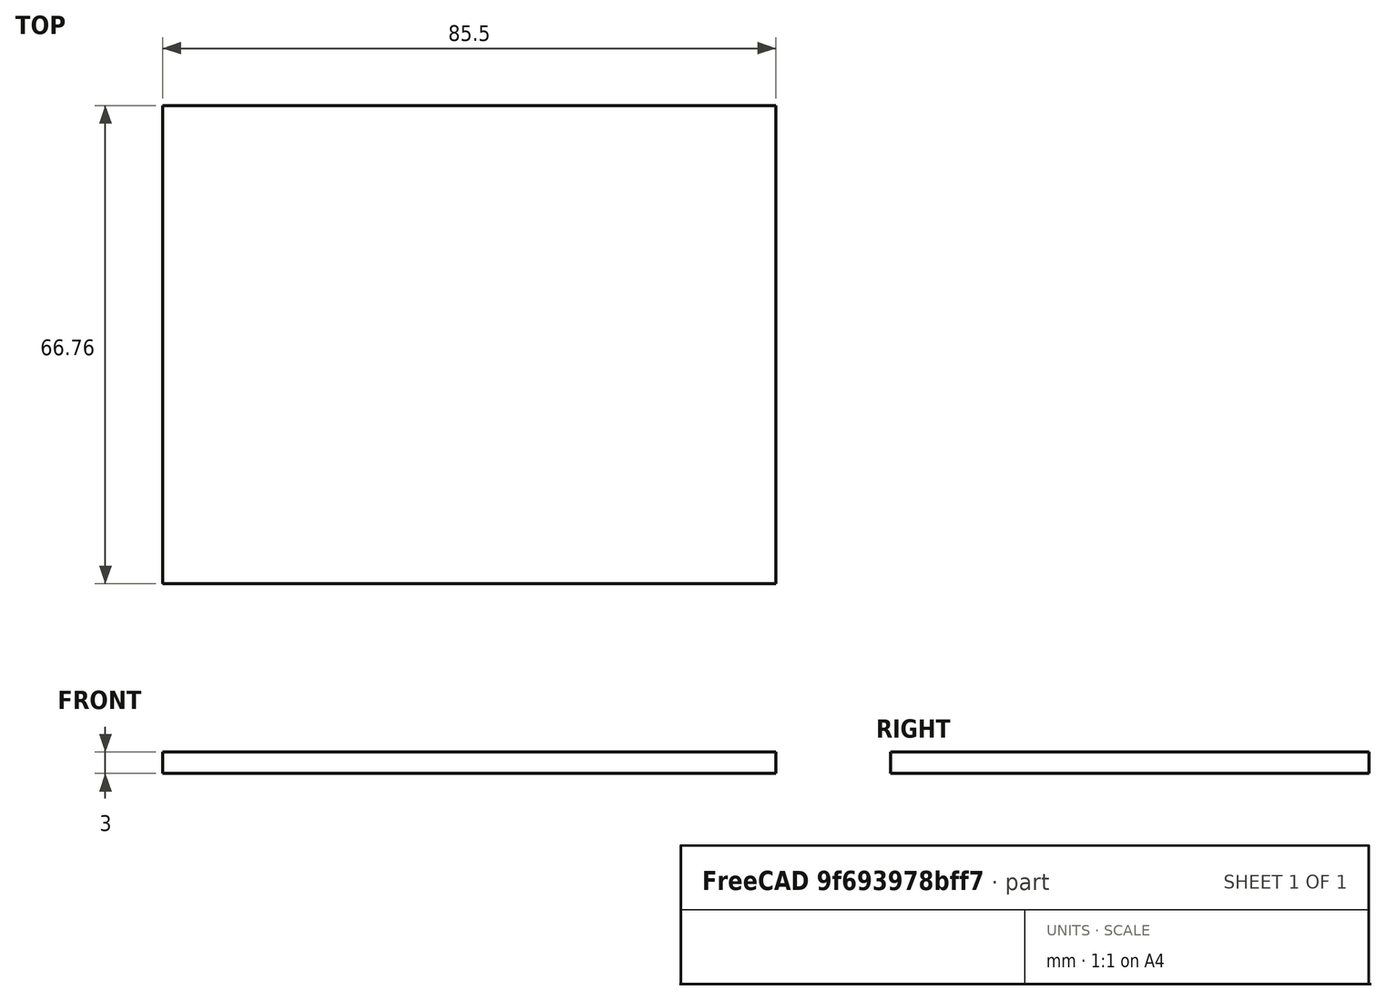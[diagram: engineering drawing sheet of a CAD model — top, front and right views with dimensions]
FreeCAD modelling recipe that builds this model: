
FCSTD DOCUMENT  (FreeCAD 1.0R39109 (Git))
Label: pcb
License: All rights reserved
LicenseURL: http://en.wikipedia.org/wiki/All_rights_reserved
objects: Sketcher::SketchObject×2, PartDesign::Pad×1, PartDesign::Body×1, App::VarSet×1
note: 8 computed .brp shape members not serialized (recipe doc carries the construction recipe); baked Part::Feature solids carry a one-line shape summary decoded from their .brp

FEATURE [Sketcher::SketchObject] Sketch
  ArcFitTolerance = 0
  AttachmentSupport = -> [XY_Plane]
  FullyConstrained = true
  MakeInternals = false
  MapMode = 5
  expr: Constraints[10] = VarSet.PCB_Width
  expr: Constraints[9] = VarSet.Ppt_PCB_Len
  sketch-geometry (4):
    g0: LineSegment StartX=-42.75 StartY=33.375 StartZ=0 EndX=42.75 EndY=33.375 EndZ=0
    g1: LineSegment StartX=42.75 StartY=33.375 StartZ=0 EndX=42.75 EndY=-33.375 EndZ=0
    g2: LineSegment StartX=42.75 StartY=-33.375 StartZ=0 EndX=-42.75 EndY=-33.375 EndZ=0
    g3: LineSegment StartX=-42.75 StartY=-33.375 StartZ=0 EndX=-42.75 EndY=33.375 EndZ=0
  constraints (11):
    c: Coincident(g0,g1)
    c: Coincident(g1,g2)
    c: Coincident(g2,g3)
    c: Coincident(g3,g0)
    c: Horizontal(g0)
    c: Horizontal(g2)
    c: Vertical(g1)
    c: Vertical(g3)
    c: Symmetric(g0,g1,g-1)
    c: DistanceX(g0,g0) = 85.5
    c: DistanceY(g1,g1) = 66.75
FEATURE [PartDesign::Pad] Pad
  Direction = (0,0,1)
  Length = 3
  Length2 = 10
  Profile = -> Sketch
  ReferenceAxis = -> Sketch [N_Axis]
  Suppressed = false
  Type = 0
FEATURE [Sketcher::SketchObject] Sketch001
  ArcFitTolerance = 0
  AttachmentSupport = -> [Pad]
  ExternalGeometry = -> [Pad]
  FullyConstrained = false
  MakeInternals = false
  MapMode = 5
  Placement = pos=(0,0,3) rot=(0,0,1;0rad)
  sketch-geometry (2):
    g0: LineSegment [constr] StartX=35.62 StartY=27.955 StartZ=0 EndX=35.62 EndY=9.6721 EndZ=0
    g1: LineSegment [constr] StartX=14.5616 StartY=27.955 StartZ=0 EndX=35.62 EndY=27.955 EndZ=0
  constraints (5):
    c: Vertical(g0)
    c: Coincident(g1,g0)
    c: Horizontal(g1)
    c: DistanceX(g0,g-3) = 7.13
    c: DistanceY(g0,g-3) = 5.42
FEATURE [PartDesign::Body] Body  label="Corps"
  AllowCompound = false
  Group = -> [Sketch,Pad,Sketch001]
  Origin = -> Origin
  Tip = -> Pad
FEATURE [App::VarSet] VarSet
  PCB_Width = 66.75
  Ppt_PCB_Len = 85.5
